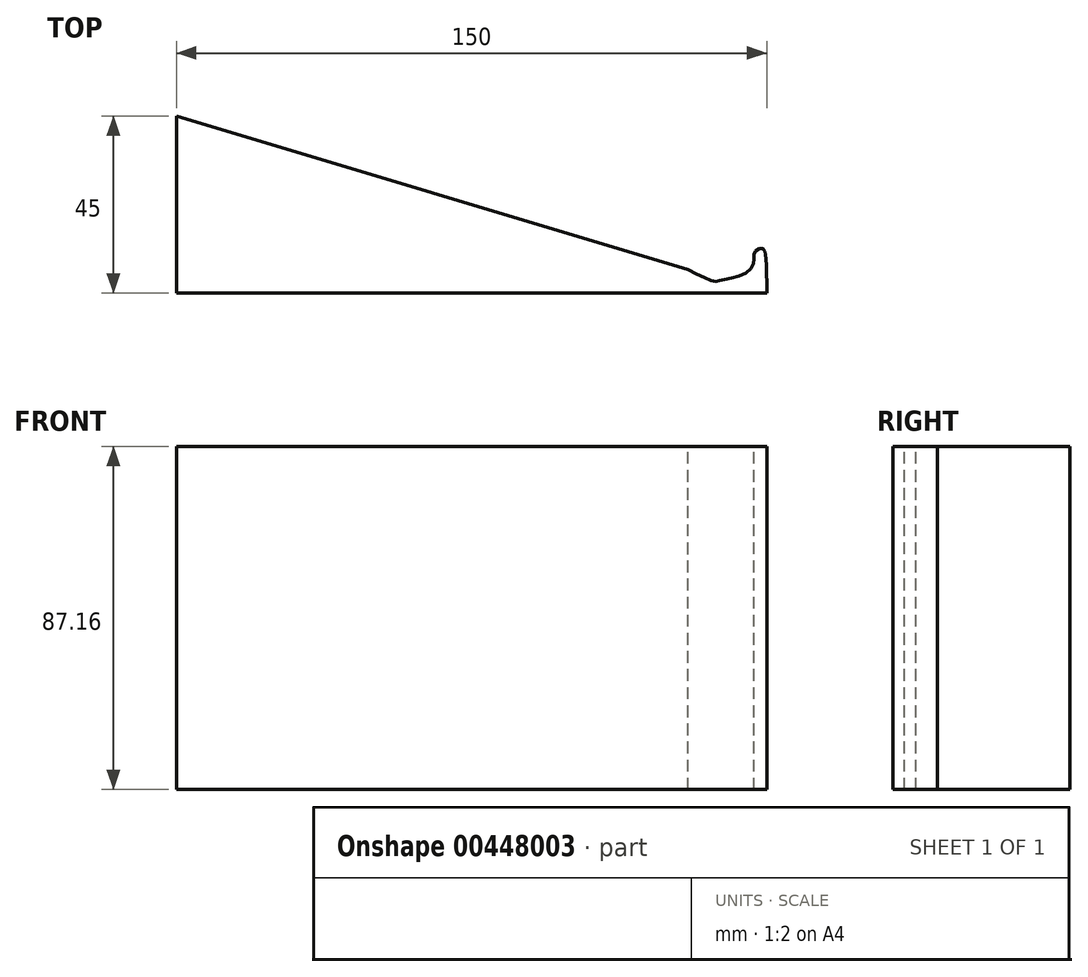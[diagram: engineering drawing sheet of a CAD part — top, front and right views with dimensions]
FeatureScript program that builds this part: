
annotation { "Feature Type Name" : "Feature", "Feature Type Description" : "" }
export const myFeature = defineFeature(function(context is Context, id is Id, definition is map)
    precondition{}
    {
        {
            var Q0;
            Q0=qCreatedBy(makeId("Top.planeOp"),FACE);
            var sketch = newSketch(context, id + "F0", { "sketchPlane" : qUnion([Q0])});
            skLineSegment(sketch, "E0", {"start": v(40.8, -64.45) * mm, "end": v(40.8, -19.45) * mm});
            skLineSegment(sketch, "E1", {"start": v(190.8, -64.45) * mm, "end": v(40.8, -64.45) * mm});
            skLineSegment(sketch, "E2", {"start": v(190.8, -64.45) * mm, "end": v(190.8, -64.45) * mm});
            skPoint(sketch, "E3.orphan", {"position": v(122.8, -37.67) * mm});
            skLineSegment(sketch, "E4", {"start": v(40.8, -19.45) * mm, "end": v(170.8, -58.51) * mm});
            skFitSpline(sketch, "E5", {"points": [v(170.8, -58.51) * mm, v(177.52, -61.45) * mm, v(179.35, -61.17) * mm, v(185.52, -59.35) * mm, v(187.54, -56.17) * mm, v(187.7, -54.04) * mm, v(189.62, -53.06) * mm, v(190.31, -53.96) * mm, v(190.63, -55.84) * mm, v(190.8, -64.45) * mm], "startDerivative": vector(50.07, -25.47) * mm, "endDerivative": vector(0.17, -58.6) * mm});
            skSolve(sketch);
        }
        {
            var Q0;
            Q0 = qSketchRegion(id + "F0", true);
            extrude(context, id + "F1", {"entities" : qUnion([Q0]), "oppositeDirection" : true, "depth" : 87.16 * mm});
        }
    });
